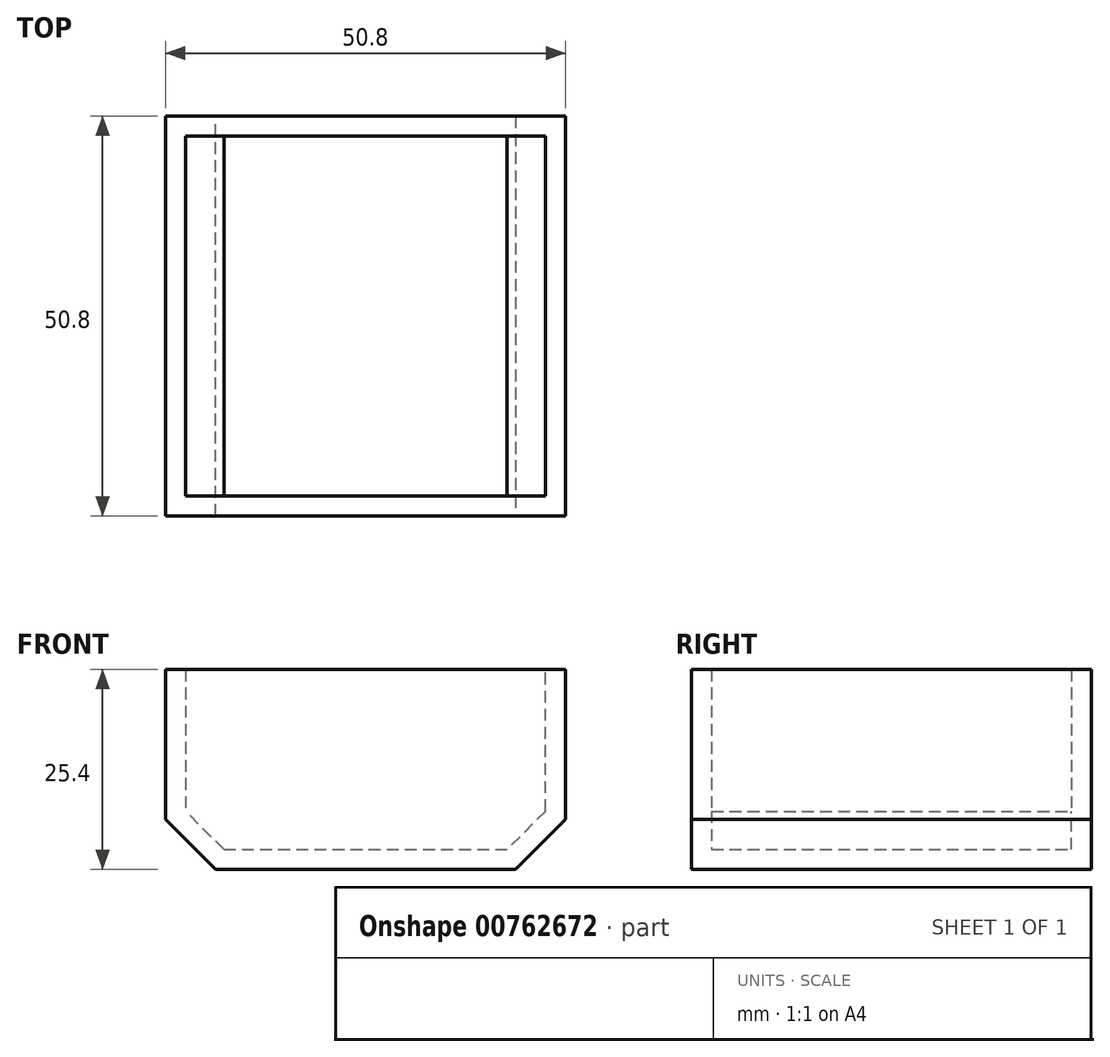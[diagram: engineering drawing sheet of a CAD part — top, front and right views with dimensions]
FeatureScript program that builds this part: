
annotation { "Feature Type Name" : "Feature", "Feature Type Description" : "" }
export const myFeature = defineFeature(function(context is Context, id is Id, definition is map)
    precondition{}
    {
        {
            var Q0;
            Q0=qCreatedBy(makeId("Front.planeOp"),FACE);
            var sketch = newSketch(context, id + "F0", { "sketchPlane" : qUnion([Q0])});
            skLineSegment(sketch, "E0", {"start": v(-80.7, -74.83) * mm, "end": v(-29.9, -74.83) * mm});
            skLineSegment(sketch, "E1", {"start": v(-29.9, -74.83) * mm, "end": v(-29.9, -49.43) * mm});
            skLineSegment(sketch, "E2", {"start": v(-29.9, -49.43) * mm, "end": v(-80.7, -49.43) * mm});
            skLineSegment(sketch, "E3", {"start": v(-80.7, -49.43) * mm, "end": v(-80.7, -74.83) * mm});
            skSolve(sketch);
        }
        {
            var Q0;
            Q0 = qSketchRegion(id + "F0", true);
            extrude(context, id + "F1", {"entities" : qUnion([Q0]), "depth" : 50.8 * mm, "offsetDistance" : 25.4 * mm});
        }
        {
            var Q0;
            Q0=makeQuery(id+"F1.opExtrude","SWEPT_EDGE",EDGE,{"disambiguationData":[OSD([sQuery(id+"F0.wireOp",EDGE,"E0"),sQuery(id+"F0.wireOp",EDGE,"E1")])]});
            chamfer(context, id + "F2", {"entities" : qUnion([Q0]), "width" : 6.35 * mm, "tangentPropagation" : true});
        }
        {
            var Q0;
            Q0=makeQuery(id+"F1.opExtrude","SWEPT_EDGE",EDGE,{"disambiguationData":[OSD([sQuery(id+"F0.wireOp",EDGE,"E0"),sQuery(id+"F0.wireOp",EDGE,"E3")])]});
            chamfer(context, id + "F3", {"entities" : qUnion([Q0]), "width" : 6.35 * mm, "tangentPropagation" : true});
        }
        {
            var Q0;
            Q0=makeQuery(id+"F1.opExtrude","SWEPT_FACE",FACE,{"disambiguationData":[OSD([sQuery(id+"F0.wireOp",EDGE,"E2")])]});
            shell(context, id + "F4", {"entities" : qUnion([Q0]), "thickness" : 2.54 * mm});
        }
    });
